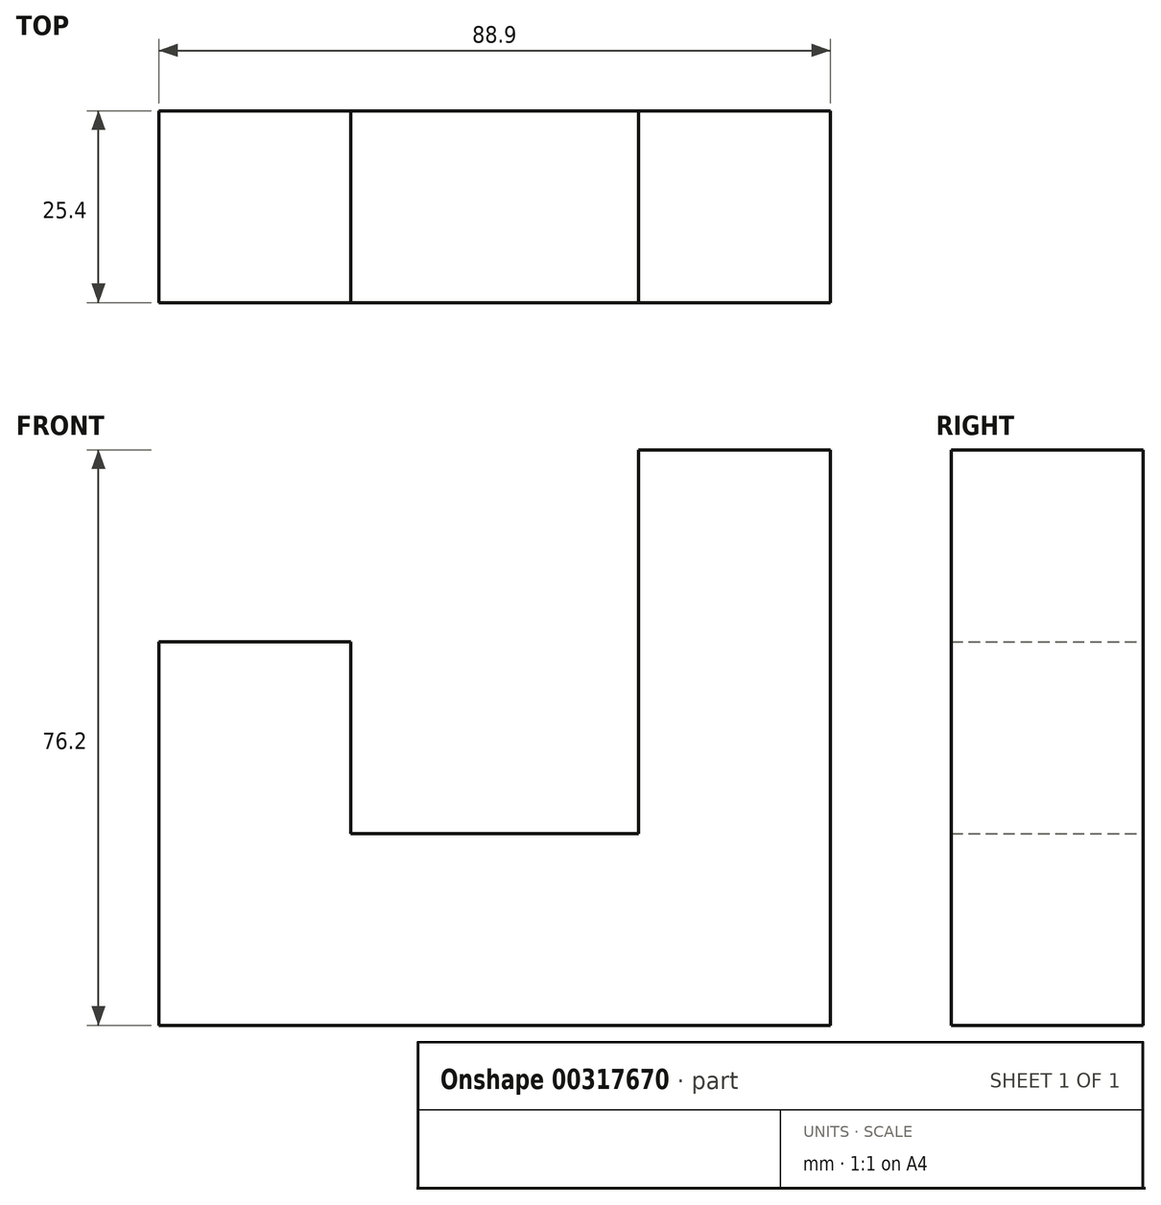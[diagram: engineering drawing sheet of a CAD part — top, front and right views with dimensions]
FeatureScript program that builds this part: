
annotation { "Feature Type Name" : "Feature", "Feature Type Description" : "" }
export const myFeature = defineFeature(function(context is Context, id is Id, definition is map)
    precondition{}
    {
        {
            var Q0;
            Q0=qCreatedBy(makeId("Front.planeOp"),FACE);
            var sketch = newSketch(context, id + "F0", { "sketchPlane" : qUnion([Q0])});
            skLineSegment(sketch, "E0", {"start": v(-40.88, -30.1) * mm, "end": v(48.02, -30.1) * mm});
            skLineSegment(sketch, "E1", {"start": v(48.02, -30.1) * mm, "end": v(48.02, 46.1) * mm});
            skLineSegment(sketch, "E2", {"start": v(48.02, 46.1) * mm, "end": v(22.62, 46.1) * mm});
            skLineSegment(sketch, "E3", {"start": v(-40.88, 20.7) * mm, "end": v(-15.48, 20.7) * mm});
            skLineSegment(sketch, "E4", {"start": v(-15.48, 20.7) * mm, "end": v(-15.48, -4.7) * mm});
            skLineSegment(sketch, "E5", {"start": v(-15.48, -4.7) * mm, "end": v(22.62, -4.7) * mm});
            skLineSegment(sketch, "E6", {"start": v(22.62, -4.7) * mm, "end": v(22.62, 46.1) * mm});
            skLineSegment(sketch, "E7", {"start": v(-40.88, 20.7) * mm, "end": v(-40.88, -30.1) * mm});
            skSolve(sketch);
        }
        {
            var Q0;
            Q0 = qSketchRegion(id + "F0", true);
            extrude(context, id + "F1", {"entities" : qUnion([Q0]), "depth" : 25.4 * mm});
        }
    });
